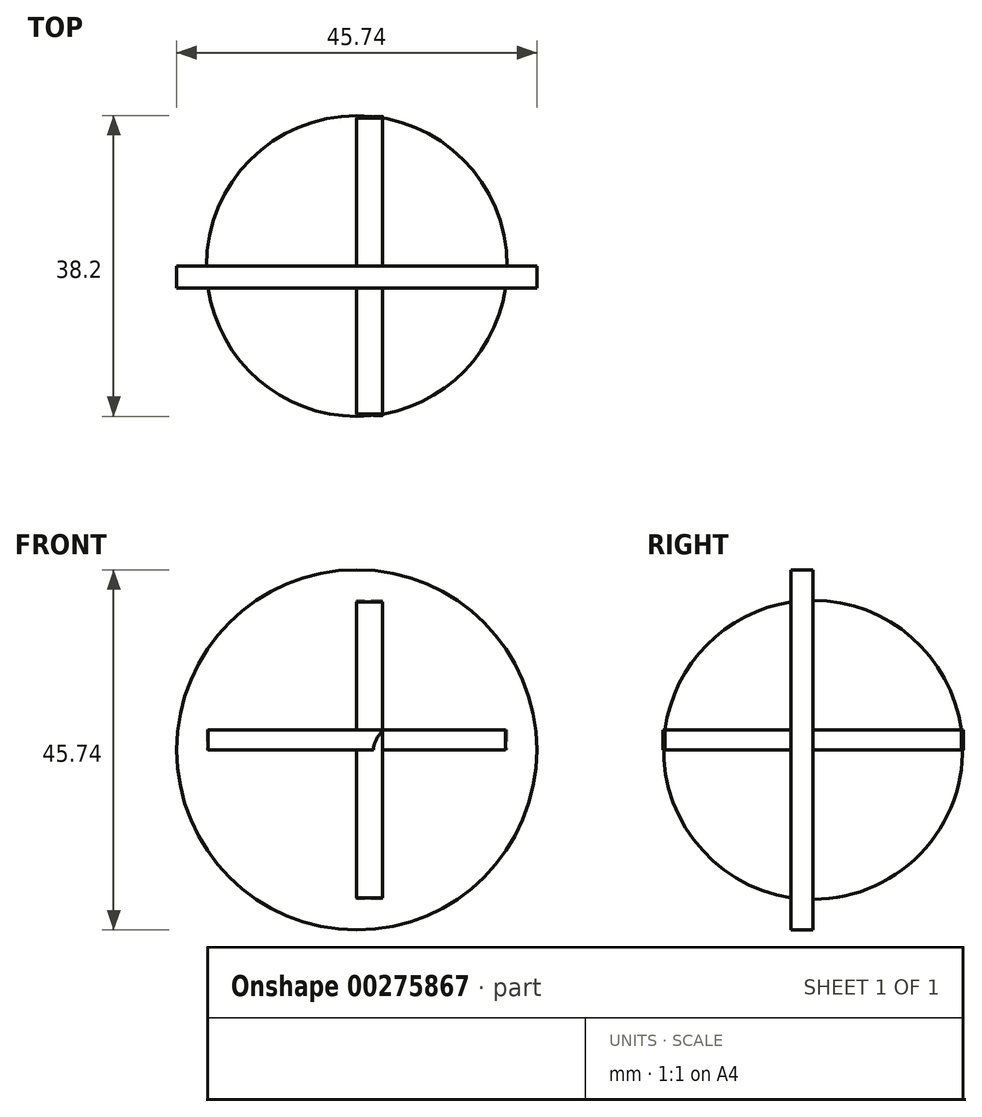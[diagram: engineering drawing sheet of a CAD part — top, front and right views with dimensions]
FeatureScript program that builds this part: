
annotation { "Feature Type Name" : "Feature", "Feature Type Description" : "" }
export const myFeature = defineFeature(function(context is Context, id is Id, definition is map)
    precondition{}
    {
        {
            var Q0;
            Q0=qCreatedBy(makeId("Top.planeOp"),FACE);
            var sketch = newSketch(context, id + "F0", { "sketchPlane" : qUnion([Q0])});
            skCircle(sketch, "E0", {"center": v(0, 0) * mm, "radius": 19.1 * mm});
            skSolve(sketch);
        }
        {
            var Q0;
            Q0 = qSketchRegion(id + "F0", true);
            extrude(context, id + "F1", {"entities" : qUnion([Q0]), "depth" : 2.54 * mm});
        }
        {
            var Q0;
            Q0=qCreatedBy(makeId("Front.planeOp"),FACE);
            var sketch = newSketch(context, id + "F2", { "sketchPlane" : qUnion([Q0])});
            skCircle(sketch, "E1", {"center": v(0, 0) * mm, "radius": 22.87 * mm});
            skSolve(sketch);
        }
        {
            var Q0;
            Q0 = qSketchRegion(id + "F2", true);
            extrude(context, id + "F3", {"entities" : qUnion([Q0]), "operationType" : NewBodyOperationType.ADD, "depth" : 2.8 * mm});
        }
        {
            var Q0;
            Q0=qCreatedBy(makeId("Right.planeOp"),FACE);
            var sketch = newSketch(context, id + "F4", { "sketchPlane" : qUnion([Q0])});
            skCircle(sketch, "E2", {"center": v(0, 0) * mm, "radius": 18.99 * mm});
            skSolve(sketch);
        }
        {
            var Q0;
            Q0 = qSketchRegion(id + "F4", true);
            extrude(context, id + "F5", {"entities" : qUnion([Q0]), "operationType" : NewBodyOperationType.ADD, "depth" : 3.3 * mm});
        }
    });
